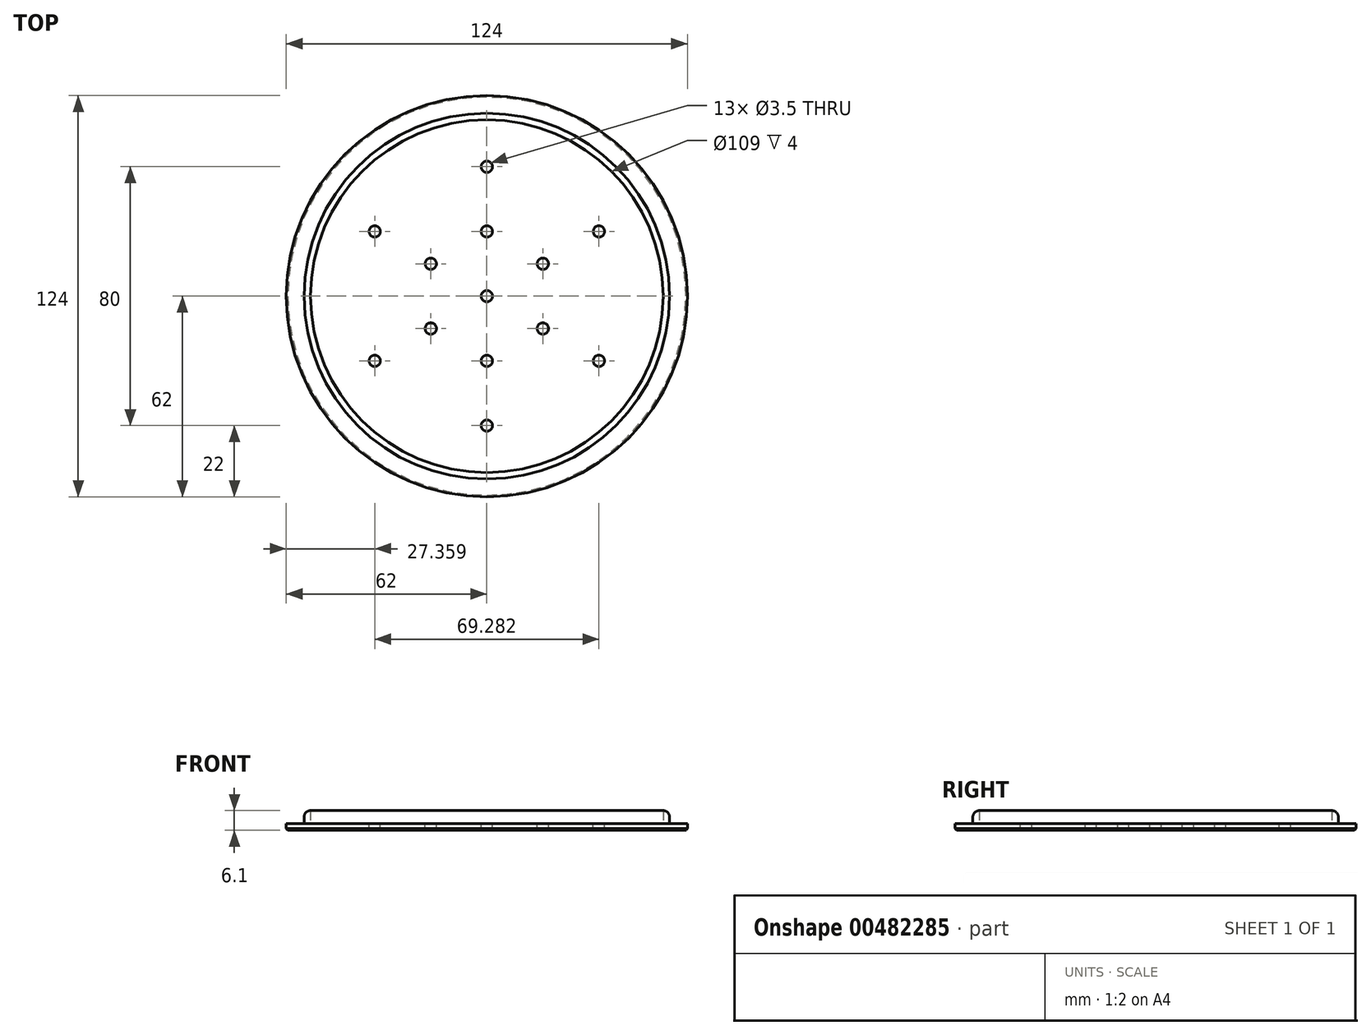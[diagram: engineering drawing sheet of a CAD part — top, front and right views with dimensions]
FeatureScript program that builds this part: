
annotation { "Feature Type Name" : "Feature", "Feature Type Description" : "" }
export const myFeature = defineFeature(function(context is Context, id is Id, definition is map)
    precondition{}
    {
        {
            var Q0;
            Q0=qCreatedBy(makeId("Top.planeOp"),FACE);
            var sketch = newSketch(context, id + "F0", { "sketchPlane" : qUnion([Q0])});
            skCircle(sketch, "E0", {"center": v(0, 0) * mm, "radius": 62 * mm});
            skSolve(sketch);
        }
        {
            var Q0;
            Q0 = qSketchRegion(id + "F0", true);
            extrude(context, id + "F1", {"entities" : qUnion([Q0]), "depth" : (7 * 0.3) * mm});
        }
        {
            var Q0;
            Q0=makeQuery(id+"F1.opExtrude","CAP_FACE",FACE,{"disambiguationData":[OSD([sQuery(id+"F0.wireOp",EDGE,"E0")])],"isStart":false});
            var sketch = newSketch(context, id + "F2", { "sketchPlane" : qUnion([Q0])});
            skCircle(sketch, "E1", {"center": v(0, 0) * mm, "radius": 56.5 * mm});
            skCircle(sketch, "E2.0", {"center": v(0, 0) * mm, "radius": 54.5 * mm});
            skSolve(sketch);
        }
        {
            var Q0;
            Q0 = qSketchRegion(id + "F2", true);
            extrude(context, id + "F3", {"entities" : qUnion([Q0]), "operationType" : NewBodyOperationType.ADD, "depth" : 4 * mm});
        }
        {
            var Q0;
            Q0=makeQuery(id+"F3.opExtrude","CAP_EDGE",EDGE,{"disambiguationData":[OSD([sQuery(id+"F2.wireOp",EDGE,"E1")])],"isStart":false});
            fillet(context, id + "F4", {"entities" : qUnion([Q0]), "radius" : 2 * mm, "tangentPropagation" : true, "allowEdgeOverflow" : false});
        }
        {
            var Q0;
            Q0=makeQuery(id+"F3.boolean.opBoolean","SPLIT",FACE,{"disambiguationData":[TD([makeQuery(id+"F3.opExtrude","SWEPT_FACE",FACE,{"disambiguationData":[OSD([sQuery(id+"F2.wireOp",EDGE,"E2.0")])]})])],"derivedFrom":makeQuery(id+"F1.opExtrude","CAP_FACE",FACE,{"disambiguationData":[OSD([sQuery(id+"F0.wireOp",EDGE,"E0")])],"isStart":false})});
            var sketch = newSketch(context, id + "F5", { "sketchPlane" : qUnion([Q0])});
            skCircle(sketch, "E3", {"center": v(0, 0) * mm, "radius": 1.75 * mm});
            skCircle(sketch, "E4", {"center": v(0, 20) * mm, "radius": 1.75 * mm});
            skCircle(sketch, "E5", {"center": v(0, 40) * mm, "radius": 1.75 * mm});
            skCircle(sketch, "E6.1.0", {"center": v(17.32, 10) * mm, "radius": 1.75 * mm});
            skCircle(sketch, "E6.1.1", {"center": v(34.64, 20) * mm, "radius": 1.75 * mm});
            skCircle(sketch, "E6.2.0", {"center": v(17.32, -10) * mm, "radius": 1.75 * mm});
            skCircle(sketch, "E6.2.1", {"center": v(34.64, -20) * mm, "radius": 1.75 * mm});
            skCircle(sketch, "E6.3.0", {"center": v(0, -20) * mm, "radius": 1.75 * mm});
            skCircle(sketch, "E6.3.1", {"center": v(0, -40) * mm, "radius": 1.75 * mm});
            skCircle(sketch, "E6.4.0", {"center": v(-17.32, -10) * mm, "radius": 1.75 * mm});
            skCircle(sketch, "E6.4.1", {"center": v(-34.64, -20) * mm, "radius": 1.75 * mm});
            skCircle(sketch, "E6.5.0", {"center": v(-17.32, 10) * mm, "radius": 1.75 * mm});
            skCircle(sketch, "E6.5.1", {"center": v(-34.64, 20) * mm, "radius": 1.75 * mm});
            skLineSegment(sketch, "E6.anchor1", {"start": v(0, 0) * mm, "end": v(0, 20) * mm, "construction": true});
            skLineSegment(sketch, "E6.anchor2", {"start": v(0, 0) * mm, "end": v(-17.32, 10) * mm, "construction": true});
            skSolve(sketch);
        }
        {
            var Q0;
            Q0 = qSketchRegion(id + "F5", true);
            extrude(context, id + "F6", {"entities" : qUnion([Q0]), "operationType" : NewBodyOperationType.REMOVE, "endBound" : BoundingType.UP_TO_NEXT, "oppositeDirection" : true, "depth" : 25 * mm});
        }
        {
            var Q0;
            Q0=makeQuery(id+"F1.opExtrude","CAP_EDGE",EDGE,{"disambiguationData":[OSD([sQuery(id+"F0.wireOp",EDGE,"E0")])],"isStart":true});
            chamfer(context, id + "F7", {"entities" : qUnion([Q0]), "width" : 0.5 * mm, "tangentPropagation" : true});
        }
    });
